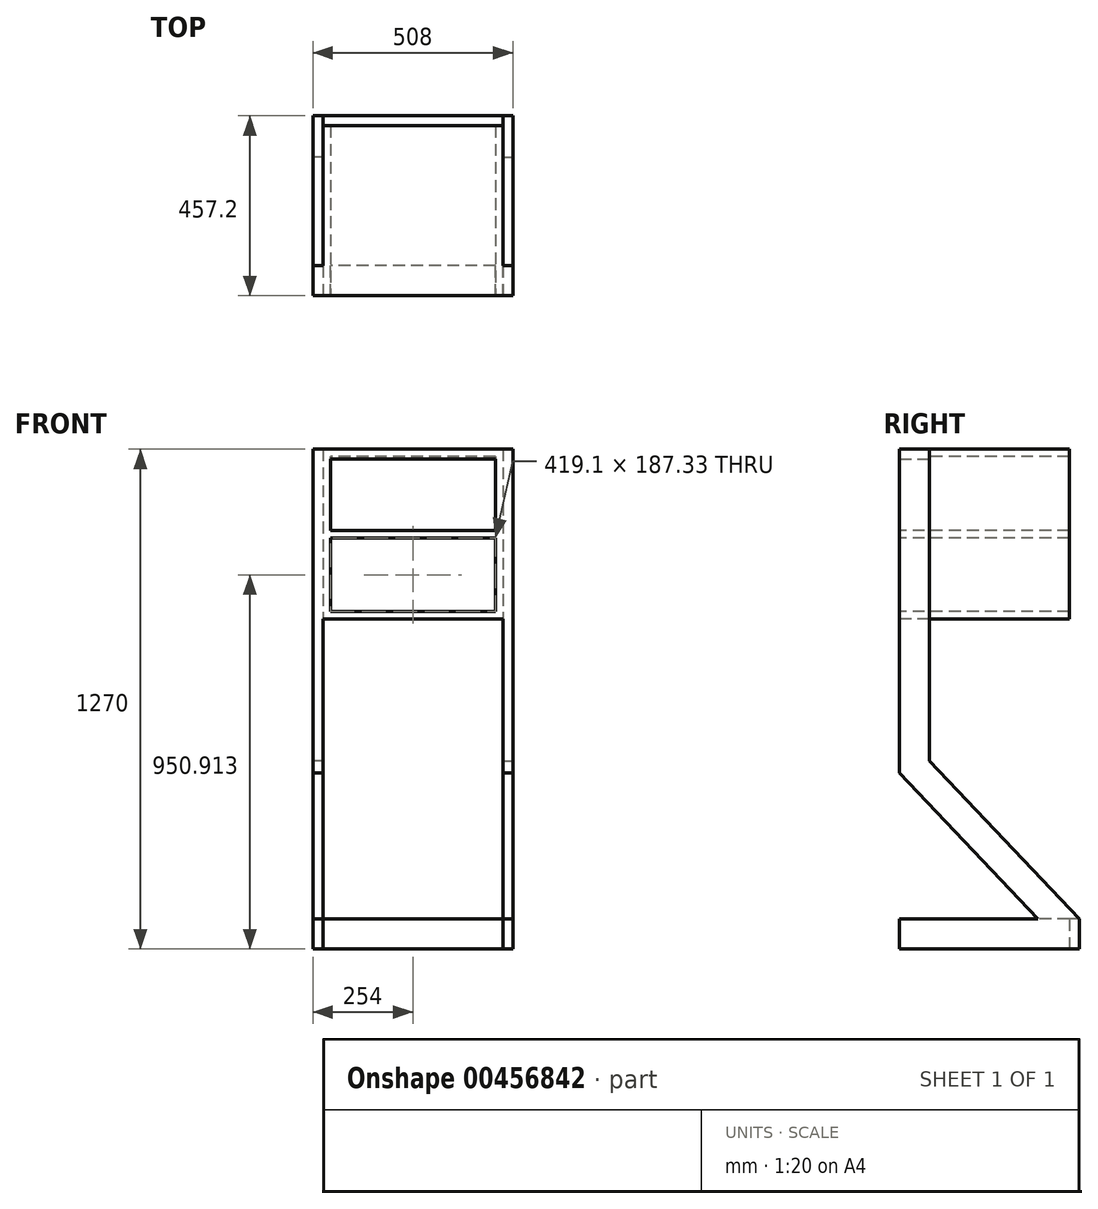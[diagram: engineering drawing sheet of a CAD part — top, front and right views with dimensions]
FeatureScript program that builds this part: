
annotation { "Feature Type Name" : "Feature", "Feature Type Description" : "" }
export const myFeature = defineFeature(function(context is Context, id is Id, definition is map)
    precondition{}
    {
        {
            var Q0;
            Q0=qCreatedBy(makeId("Top.planeOp"),FACE);
            var sketch = newSketch(context, id + "F0", { "sketchPlane" : qUnion([Q0])});
            skLineSegment(sketch, "E0", {"start": v(0, 228.6) * mm, "end": v(0, -228.6) * mm, "construction": true});
            skLineSegment(sketch, "E1.bottom", {"start": v(-254, -228.6) * mm, "end": v(254, -228.6) * mm, "construction": true});
            skLineSegment(sketch, "E1.top", {"start": v(-254, 228.6) * mm, "end": v(254, 228.6) * mm, "construction": true});
            skLineSegment(sketch, "E1.left", {"start": v(-254, -228.6) * mm, "end": v(-254, 228.6) * mm, "construction": true});
            skLineSegment(sketch, "E1.right", {"start": v(254, -228.6) * mm, "end": v(254, 228.6) * mm, "construction": true});
            skPoint(sketch, "E1.middle", {"position": v(0, 0) * mm});
            skLineSegment(sketch, "E2", {"start": v(254, -228.6) * mm, "end": v(228.6, -228.6) * mm});
            skLineSegment(sketch, "E3", {"start": v(228.6, -228.6) * mm, "end": v(229.07, 203.2) * mm});
            skLineSegment(sketch, "E4", {"start": v(229.07, 203.2) * mm, "end": v(-228.6, 203.2) * mm});
            skLineSegment(sketch, "E5", {"start": v(-228.6, 203.2) * mm, "end": v(-228.6, -228.6) * mm});
            skPoint(sketch, "E5.endSnap0", {"position": v(0, -228.6) * mm});
            skLineSegment(sketch, "E6", {"start": v(-228.6, -228.6) * mm, "end": v(-254, -228.6) * mm});
            skLineSegment(sketch, "E7", {"start": v(-254, 228.6) * mm, "end": v(-254, 228.6) * mm});
            skLineSegment(sketch, "E8", {"start": v(-254, -228.6) * mm, "end": v(-254, 228.6) * mm});
            skLineSegment(sketch, "E9", {"start": v(-254, 228.6) * mm, "end": v(254, 228.6) * mm});
            skLineSegment(sketch, "E10", {"start": v(254, 228.6) * mm, "end": v(254, -228.6) * mm});
            skLineSegment(sketch, "E11", {"start": v(-633.3, -57.95) * mm, "end": v(-633.3, -57.95) * mm});
            skSolve(sketch);
        }
        {
            var Q0;
            Q0=makeQuery(id+"F0.imprint","IMPRINT",FACE,{"disambiguationData":[TD([[makeQuery(id+"F0.imprint","IMPRINT",EDGE,{"derivedFrom":sQuery(id+"F0.wireOp",EDGE,"E2")}),-1.0]])]});
            extrude(context, id + "F1", {"entities" : qUnion([Q0]), "depth" : 76.2 * mm});
        }
        {
            var Q0;
            Q0=qCreatedBy(makeId("Top.planeOp"),FACE);
            cPlane(context, id + "F2", {"entities" : qUnion([Q0]), "cplaneType" : CPlaneType.OFFSET, "offset" : 76.2 * mm, "width" : 152.4 * mm, "height" : 152.4 * mm});
        }
        {
            var Q0;
            Q0=qCreatedBy(makeId("Right.planeOp"),FACE);
            cPlane(context, id + "F3", {"entities" : qUnion([Q0]), "cplaneType" : CPlaneType.OFFSET, "offset" : 254 * mm, "width" : 152.4 * mm, "height" : 152.4 * mm});
        }
        {
            var Q0;
            Q0=qCreatedBy(id+"F3.planeOp",FACE);
            var sketch = newSketch(context, id + "F4", { "sketchPlane" : qUnion([Q0])});
            skLineSegment(sketch, "E12", {"start": v(-228.6, 76.2) * mm, "end": v(228.6, 76.2) * mm, "construction": true});
            skLineSegment(sketch, "E13", {"start": v(0, 400.78) * mm, "end": v(0, -344.45) * mm, "construction": true});
            skLineSegment(sketch, "E14", {"start": v(-228.6, 76.2) * mm, "end": v(-228.6, 558.8) * mm, "construction": true});
            skLineSegment(sketch, "E15", {"start": v(228.6, 76.2) * mm, "end": v(-152.4, 478.37) * mm});
            skLineSegment(sketch, "E16", {"start": v(123.63, 76.2) * mm, "end": v(-228.6, 448) * mm});
            skLineSegment(sketch, "E17", {"start": v(-228.6, 448) * mm, "end": v(-152.4, 448) * mm, "construction": true});
            skLineSegment(sketch, "E18", {"start": v(-152.4, 1244.6) * mm, "end": v(-152.4, 448) * mm});
            skLineSegment(sketch, "E19", {"start": v(-152.4, 1244.6) * mm, "end": v(-228.6, 1244.6) * mm});
            skLineSegment(sketch, "E20", {"start": v(-228.6, 1244.6) * mm, "end": v(-228.6, 448) * mm});
            skLineSegment(sketch, "E21", {"start": v(228.6, 76.2) * mm, "end": v(123.63, 76.2) * mm});
            skSolve(sketch);
        }
        {
            var Q0;
            {var subQ2=sQuery(id+"F4.wireOp",EDGE,"E15");Q0=makeQuery(id+"F4.imprint","IMPRINT",FACE,{"disambiguationData":[TD([[makeQuery(id+"F4.imprint","IMPRINT",EDGE,{"derivedFrom":subQ2}),1.0]])]});}
            extrude(context, id + "F5", {"entities" : qUnion([Q0]), "operationType" : NewBodyOperationType.ADD, "oppositeDirection" : true, "depth" : 25.4 * mm});
        }
        {
            var Q0;
            Q0=qCreatedBy(makeId("Right.planeOp"),FACE);
            cPlane(context, id + "F6", {"entities" : qUnion([Q0]), "cplaneType" : CPlaneType.OFFSET, "offset" : 254 * mm, "oppositeDirection" : true, "width" : 152.4 * mm, "height" : 152.4 * mm});
        }
        {
            var Q0;
            Q0=qCreatedBy(id+"F6.planeOp",FACE);
            var sketch = newSketch(context, id + "F7", { "sketchPlane" : qUnion([Q0])});
            skLineSegment(sketch, "E22", {"start": v(-228.6, 76.2) * mm, "end": v(228.6, 76.2) * mm, "construction": true});
            skLineSegment(sketch, "E23", {"start": v(0, 400.78) * mm, "end": v(0, -344.45) * mm, "construction": true});
            skLineSegment(sketch, "E24", {"start": v(-228.6, 76.2) * mm, "end": v(-228.6, 558.8) * mm, "construction": true});
            skLineSegment(sketch, "E25", {"start": v(228.6, 76.2) * mm, "end": v(-152.4, 478.37) * mm});
            skLineSegment(sketch, "E26", {"start": v(123.63, 76.2) * mm, "end": v(-228.6, 448) * mm});
            skLineSegment(sketch, "E27", {"start": v(-228.6, 448) * mm, "end": v(-152.4, 448) * mm, "construction": true});
            skLineSegment(sketch, "E28", {"start": v(-152.4, 1244.6) * mm, "end": v(-152.4, 448) * mm});
            skLineSegment(sketch, "E29", {"start": v(-152.4, 1244.6) * mm, "end": v(-228.6, 1244.6) * mm});
            skLineSegment(sketch, "E30", {"start": v(-228.6, 1244.6) * mm, "end": v(-228.6, 448) * mm});
            skLineSegment(sketch, "E31", {"start": v(228.6, 76.2) * mm, "end": v(123.63, 76.2) * mm});
            skLineSegment(sketch, "E32", {"start": v(-228.6, 0) * mm, "end": v(228.6, 0) * mm, "construction": true});
            skLineSegment(sketch, "E33", {"start": v(228.6, 0) * mm, "end": v(228.6, 0) * mm});
            skLineSegment(sketch, "E34", {"start": v(-228.6, 0) * mm, "end": v(-228.6, 76.2) * mm, "construction": true});
            skSolve(sketch);
        }
        {
            var Q0;
            {var subQ2=sQuery(id+"F7.wireOp",EDGE,"E25");Q0=makeQuery(id+"F7.imprint","IMPRINT",FACE,{"disambiguationData":[TD([[makeQuery(id+"F7.imprint","IMPRINT",EDGE,{"derivedFrom":subQ2}),1.0]])]});}
            extrude(context, id + "F8", {"entities" : qUnion([Q0]), "operationType" : NewBodyOperationType.ADD, "depth" : 25.4 * mm});
        }
        {
            var Q0;
            Q0=qCreatedBy(makeId("Front.planeOp"),FACE);
            cPlane(context, id + "F9", {"entities" : qUnion([Q0]), "cplaneType" : CPlaneType.OFFSET, "offset" : 228.6 * mm, "width" : 152.4 * mm, "height" : 152.4 * mm});
        }
        {
            var Q0;
            Q0=qCreatedBy(id+"F9.planeOp",FACE);
            var sketch = newSketch(context, id + "F10", { "sketchPlane" : qUnion([Q0])});
            skLineSegment(sketch, "E35", {"start": v(0, 0) * mm, "end": v(0, 1270) * mm, "construction": true});
            skLineSegment(sketch, "E36", {"start": v(228.6, 1270) * mm, "end": v(-228.6, 1270) * mm, "construction": true});
            skLineSegment(sketch, "E37", {"start": v(228.6, 1270) * mm, "end": v(228.6, 838.2) * mm, "construction": true});
            skLineSegment(sketch, "E38.bottom", {"start": v(-228.6, 1270) * mm, "end": v(228.6, 1270) * mm});
            skLineSegment(sketch, "E38.top", {"start": v(-228.6, 838.2) * mm, "end": v(228.6, 838.2) * mm});
            skLineSegment(sketch, "E38.left", {"start": v(-228.6, 1270) * mm, "end": v(-228.6, 838.2) * mm});
            skLineSegment(sketch, "E38.right", {"start": v(228.6, 1270) * mm, "end": v(228.6, 838.2) * mm});
            skLineSegment(sketch, "E39.bottom", {"start": v(-209.55, 1250.95) * mm, "end": v(209.55, 1250.95) * mm});
            skLineSegment(sketch, "E39.top", {"start": v(-209.55, 857.25) * mm, "end": v(209.55, 857.25) * mm});
            skLineSegment(sketch, "E39.left", {"start": v(-209.55, 1250.95) * mm, "end": v(-209.55, 1063.62) * mm});
            skLineSegment(sketch, "E39.right", {"start": v(209.55, 1250.95) * mm, "end": v(209.55, 1063.62) * mm});
            skPoint(sketch, "E39.middle", {"position": v(0, 1054.1) * mm});
            skLineSegment(sketch, "E40.bottom", {"start": v(-209.55, 1063.62) * mm, "end": v(209.55, 1063.62) * mm});
            skLineSegment(sketch, "E40.top", {"start": v(-209.55, 1044.58) * mm, "end": v(209.55, 1044.58) * mm});
            skLineSegment(sketch, "E41.trimOffspring", {"start": v(-209.55, 1044.58) * mm, "end": v(-209.55, 857.25) * mm});
            skLineSegment(sketch, "E42.trimOffspring", {"start": v(209.55, 1044.58) * mm, "end": v(209.55, 857.25) * mm});
            skSolve(sketch);
        }
        {
            var Q0;
            Q0=makeQuery(id+"F10.imprint","IMPRINT",FACE,{"disambiguationData":[TD([[makeQuery(id+"F10.imprint","IMPRINT",EDGE,{"derivedFrom":sQuery(id+"F10.wireOp",EDGE,"E38.bottom")}),-1.0]])]});
            extrude(context, id + "F11", {"entities" : qUnion([Q0]), "operationType" : NewBodyOperationType.ADD, "oppositeDirection" : true, "depth" : 431.8 * mm});
        }
        {
            var Q0;
            Q0=qCreatedBy(id+"F3.planeOp",FACE);
            var sketch = newSketch(context, id + "F12", { "sketchPlane" : qUnion([Q0])});
            skLineSegment(sketch, "E43", {"start": v(0, 1244.6) * mm, "end": v(0, 0) * mm, "construction": true});
            skLineSegment(sketch, "E44", {"start": v(0, 1244.6) * mm, "end": v(-228.6, 1244.6) * mm, "construction": true});
            skLineSegment(sketch, "E45.bottom", {"start": v(-152.4, 1270) * mm, "end": v(-228.6, 1270) * mm});
            skLineSegment(sketch, "E45.top", {"start": v(-152.4, 1244.6) * mm, "end": v(-228.6, 1244.6) * mm});
            skLineSegment(sketch, "E45.left", {"start": v(-152.4, 1270) * mm, "end": v(-152.4, 1244.6) * mm});
            skLineSegment(sketch, "E45.right", {"start": v(-228.6, 1270) * mm, "end": v(-228.6, 1244.6) * mm});
            skSolve(sketch);
        }
        {
            var Q0;
            Q0=makeQuery(id+"F12.imprint","IMPRINT",FACE,{"disambiguationData":[TD([[makeQuery(id+"F12.imprint","IMPRINT",EDGE,{"derivedFrom":sQuery(id+"F12.wireOp",EDGE,"E45.bottom")}),1.0]])]});
            extrude(context, id + "F13", {"entities" : qUnion([Q0]), "operationType" : NewBodyOperationType.ADD, "oppositeDirection" : true, "depth" : 508 * mm});
        }
    });
